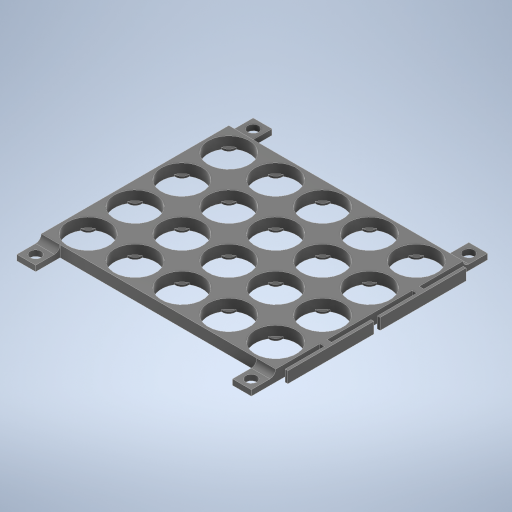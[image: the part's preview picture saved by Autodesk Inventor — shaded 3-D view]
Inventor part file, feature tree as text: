
AUTODESK INVENTOR PART (.ipt)
format: ipt  version: 2024.2 (Build 282272000, 272)  size: 567,808 bytes
history: native  units: in
note: dims shown in document units (in); Inventor stores cm internally (conversion verified against a paired STEP export)
features: sketch x4, extrude x4, pattern_linear x2, fillet x1, hole x1
ambient origin geometry x8: Origin, YZ Plane, XZ Plane, XY Plane, X Axis, Y Axis, Z Axis, Center Point
bodies: Body1 (feature_tree)
feature tree (12):
  sketch  "Sketch1"  dims[d18=0.0in d20=0.0in]
  extrude  "thickness"  TaperAngle=0.0deg  [1 undecoded]
  extrude  "catcher"  Depth=0.2756in
  pattern_linear  "gridPattern"  Count1=5 Spacing1=0.9843in
  extrude  "clasp"  Depth=0.9843in
  extrude  "Extrusion5"  Depth=0.9843in
  fillet  "Fillet1"  Radius=0.0984in
  hole  "Hole1"  [1 undecoded]
  pattern_linear  "Rectangular Pattern3"  Spacing1=0.2362in  [1 undecoded]
  sketch  "Sketch2"  dims[d27=0.2756in d28=0.2756in]
  sketch  "Sketch3"  dims[d29=0.2756in d30=1.9685in d32=0.9843in]
  sketch  "Sketch4"  dims[d33=1.5748in d35=0.9843in d36=0.9843in d37=0.9843in d41=0.0984in d43=0.0591in d44=0.2362in d45=0.0in d46=0.3937in d47=0.5118in d49=0.1181in d50=0.0in d51=0.1181in d52=0.2362in d53=0.75in d54=0.375in d55=0.25in d56=0.5635in d57=1.0in d58=0.0in d59=0.7874in d61=4.5273in d62=0.7874in d64=4.5673in d17=0.5in d19=0.5in d21=0.5in d22=0.0344in d31=0.0344in d38=0.5in d39=0.0344in d40=0.5in]
note: 3 required parameter values undecoded (feature->parameter linkage not recoverable at this tier; creation-order binding heuristic only, values carry confidence <= 0.55)
